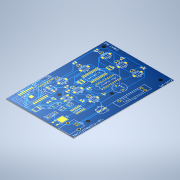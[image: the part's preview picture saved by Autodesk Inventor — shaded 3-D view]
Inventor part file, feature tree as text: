
AUTODESK INVENTOR PART (.ipt)
format: ipt  version: 2020 (Build 240168000, 168)  size: 353,792 bytes
history: native  units: in
note: dims shown in document units (in); Inventor stores cm internally (conversion verified against a paired STEP export)
features: sketch x3, other x2, extrude x1
ambient origin geometry x8: Origin, YZ Plane, XZ Plane, XY Plane, X Axis, Y Axis, Z Axis, Center Point
bodies: Solid1 (feature_tree)
feature tree (6):
  extrude  "Extrusion1"  Depth=2.9449in
  other  "Decal1"
  sketch  "Sketch3"  dims[d6=4.335in]
  sketch  "Sketch1"  dims[d0=4.335in d1=2.9449in]
  sketch  "Sketch2"  dims[d2=0.0394in d3=0.0in]
  other  "Image1"
